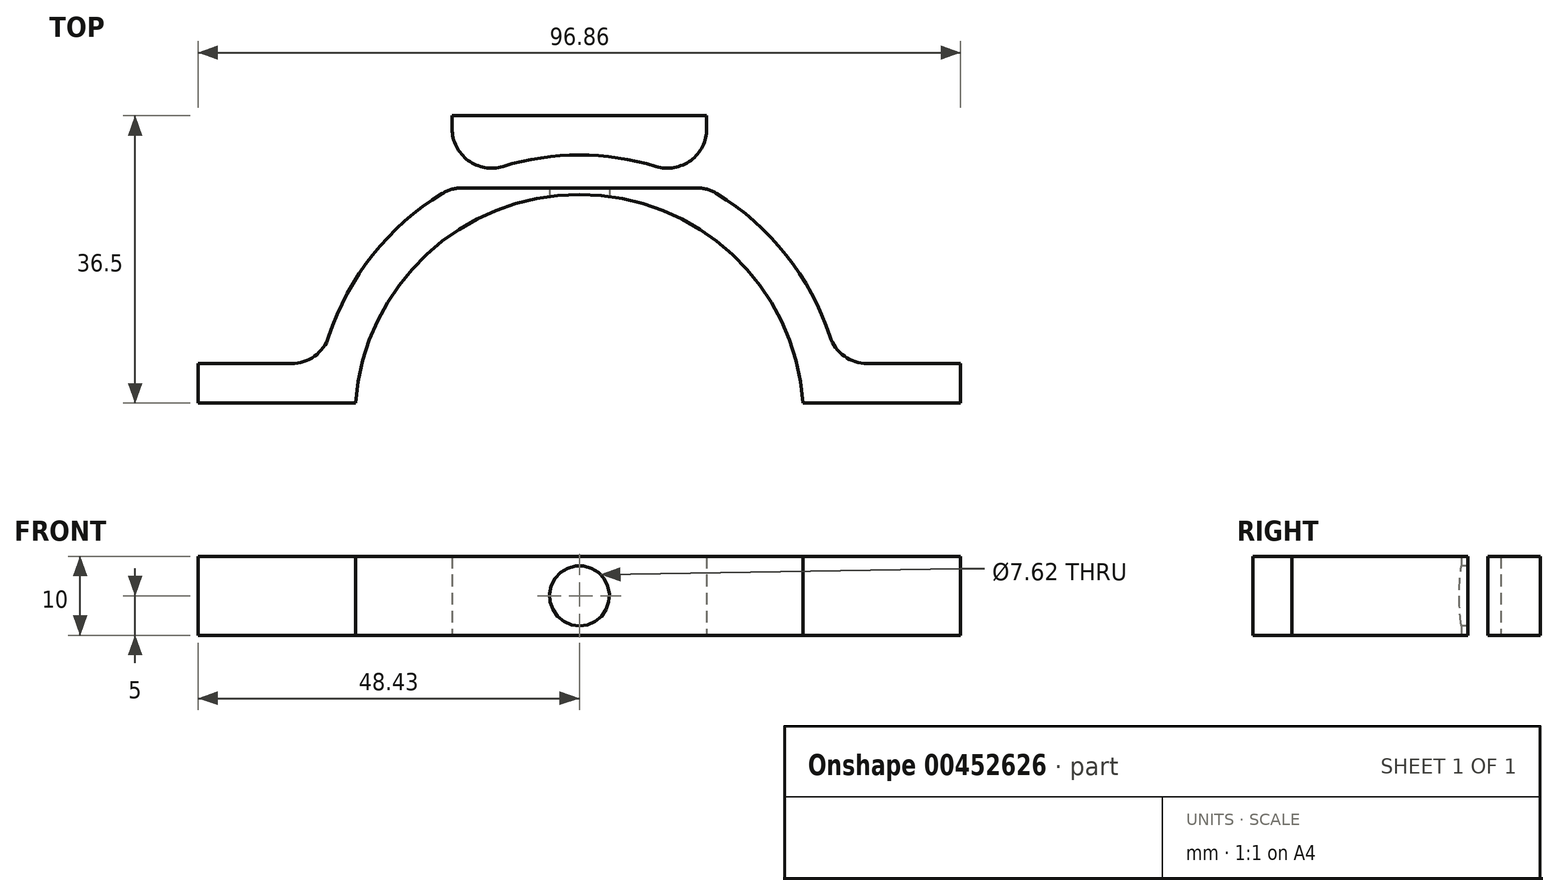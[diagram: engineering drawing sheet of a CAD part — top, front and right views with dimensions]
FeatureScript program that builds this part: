
annotation { "Feature Type Name" : "Feature", "Feature Type Description" : "" }
export const myFeature = defineFeature(function(context is Context, id is Id, definition is map)
    precondition{}
    {
        {
            var Q0;
            Q0=qCreatedBy(makeId("Top.planeOp"),FACE);
            var sketch = newSketch(context, id + "F0", { "sketchPlane" : qUnion([Q0])});
            skCircle(sketch, "E0", {"center": v(0, 0) * mm, "radius": 28.5 * mm, "construction": true});
            skLineSegment(sketch, "E1", {"start": v(-71.53, 0) * mm, "end": v(71.36, 0) * mm, "construction": true});
            skLineSegment(sketch, "E2", {"start": v(-71.7, 2) * mm, "end": v(71.19, 2) * mm, "construction": true});
            skArc(sketch, "E3", {"start": v(28.43, 2) * mm, "mid": v(0, 28.5) * mm, "end": v(-28.43, 2) * mm});
            skArc(sketch, "E4", {"start": v(33.44, 2) * mm, "mid": v(0, 33.5) * mm, "end": v(-33.44, 2) * mm});
            skLineSegment(sketch, "E5", {"start": v(-33.44, 2) * mm, "end": v(-28.43, 2) * mm});
            skLineSegment(sketch, "E6", {"start": v(28.43, 2) * mm, "end": v(33.44, 2) * mm});
            skLineSegment(sketch, "E7.bottom", {"start": v(-28.43, 2) * mm, "end": v(-48.43, 2) * mm});
            skLineSegment(sketch, "E7.top", {"start": v(-28.43, 7) * mm, "end": v(-48.43, 7) * mm});
            skLineSegment(sketch, "E7.left", {"start": v(-28.43, 2) * mm, "end": v(-28.43, 7) * mm});
            skLineSegment(sketch, "E7.right", {"start": v(-48.43, 2) * mm, "end": v(-48.43, 7) * mm});
            skLineSegment(sketch, "E8.bottom", {"start": v(28.43, 2) * mm, "end": v(48.43, 2) * mm});
            skLineSegment(sketch, "E8.top", {"start": v(28.43, 7) * mm, "end": v(48.43, 7) * mm});
            skLineSegment(sketch, "E8.left", {"start": v(28.43, 2) * mm, "end": v(28.43, 7) * mm});
            skLineSegment(sketch, "E8.right", {"start": v(48.43, 2) * mm, "end": v(48.43, 7) * mm});
            skLineSegment(sketch, "E9.bottom", {"start": v(-16.17, 33.5) * mm, "end": v(16.17, 33.5) * mm});
            skLineSegment(sketch, "E9.top", {"start": v(-16.17, 29.34) * mm, "end": v(16.17, 29.34) * mm});
            skLineSegment(sketch, "E9.left", {"start": v(-16.17, 33.5) * mm, "end": v(-16.17, 29.34) * mm});
            skLineSegment(sketch, "E9.right", {"start": v(16.17, 33.5) * mm, "end": v(16.17, 29.34) * mm});
            skPoint(sketch, "E10", {"position": v(0, 33.5) * mm});
            skLineSegment(sketch, "E11.top", {"start": v(-16.17, 23.47) * mm, "end": v(16.17, 23.47) * mm});
            skLineSegment(sketch, "E11.left", {"start": v(-16.17, 29.34) * mm, "end": v(-16.17, 23.47) * mm});
            skLineSegment(sketch, "E11.right", {"start": v(16.17, 29.34) * mm, "end": v(16.17, 23.47) * mm});
            skLineSegment(sketch, "E12.top", {"start": v(-16.17, 38.5) * mm, "end": v(16.17, 38.5) * mm});
            skLineSegment(sketch, "E12.left", {"start": v(-16.17, 33.5) * mm, "end": v(-16.17, 38.5) * mm});
            skLineSegment(sketch, "E12.right", {"start": v(16.17, 33.5) * mm, "end": v(16.17, 38.5) * mm});
            skSolve(sketch);
        }
        {
            var Q0;
            Q0=makeQuery(id+"F0.imprint","IMPRINT",FACE,{"disambiguationData":[TD([[makeQuery(id+"F0.imprint","IMPRINT",EDGE,{"derivedFrom":sQuery(id+"F0.wireOp",EDGE,"E3")}),-1.0]])]});
            var Q1;
            {var subQ5=sQuery(id+"F0.wireOp",EDGE,"E7.right");Q1=makeQuery(id+"F0.imprint","IMPRINT",FACE,{"disambiguationData":[TD([[makeQuery(id+"F0.imprint","IMPRINT",EDGE,{"derivedFrom":subQ5}),-1.0]])]});}
            var Q2;
            {var subQ5=sQuery(id+"F0.wireOp",EDGE,"E7.left");Q2=makeQuery(id+"F0.imprint","IMPRINT",FACE,{"disambiguationData":[TD([[makeQuery(id+"F0.imprint","IMPRINT",EDGE,{"derivedFrom":subQ5}),1.0]])]});}
            var Q3;
            {var subQ5=sQuery(id+"F0.wireOp",EDGE,"E8.left");Q3=makeQuery(id+"F0.imprint","IMPRINT",FACE,{"disambiguationData":[TD([[makeQuery(id+"F0.imprint","IMPRINT",EDGE,{"derivedFrom":subQ5}),-1.0]])]});}
            var Q4;
            {var subQ5=sQuery(id+"F0.wireOp",EDGE,"E8.right");Q4=makeQuery(id+"F0.imprint","IMPRINT",FACE,{"disambiguationData":[TD([[makeQuery(id+"F0.imprint","IMPRINT",EDGE,{"derivedFrom":subQ5}),1.0]])]});}
            var Q5;
            {var subQ0=sQuery(id+"F0.wireOp",EDGE,"E9.left");Q5=makeQuery(id+"F0.imprint","IMPRINT",FACE,{"disambiguationData":[TD([[makeQuery(id+"F0.imprint","IMPRINT",EDGE,{"derivedFrom":subQ0}),1.0]])]});}
            var Q6;
            {var subQ0=sQuery(id+"F0.wireOp",EDGE,"E9.right");Q6=makeQuery(id+"F0.imprint","IMPRINT",FACE,{"disambiguationData":[TD([[makeQuery(id+"F0.imprint","IMPRINT",EDGE,{"derivedFrom":subQ0}),-1.0]])]});}
            var Q7;
            {var subQ0=sQuery(id+"F0.wireOp",EDGE,"E7.left");Q7=makeQuery(id+"F0.imprint","IMPRINT",FACE,{"disambiguationData":[TD([[makeQuery(id+"F0.imprint","IMPRINT",EDGE,{"derivedFrom":subQ0}),-1.0]])]});}
            var Q8;
            {var subQ0=sQuery(id+"F0.wireOp",EDGE,"E9.top");var subQ4=sQuery(id+"F0.wireOp",EDGE,"E3");var subQ7=makeQuery(id+"F0.imprint","INTERSECT",VERTEX,{"disambiguationData":[OD(0.0)],"derivedFrom":[subQ4,subQ0]});Q8=makeQuery(id+"F0.imprint","IMPRINT",FACE,{"disambiguationData":[TD([[makeQuery(id+"F0.imprint","IMPRINT",EDGE,{"disambiguationData":[TD([[subQ7,-1.0]])],"derivedFrom":subQ4}),-1.0]])]});}
            var Q9;
            {var subQ0=sQuery(id+"F0.wireOp",EDGE,"E11.top");Q9=makeQuery(id+"F0.imprint","IMPRINT",FACE,{"disambiguationData":[TD([[makeQuery(id+"F0.imprint","IMPRINT",EDGE,{"derivedFrom":subQ0}),1.0]])]});}
            var Q10;
            {var subQ0=sQuery(id+"F0.wireOp",EDGE,"E8.left");Q10=makeQuery(id+"F0.imprint","IMPRINT",FACE,{"disambiguationData":[TD([[makeQuery(id+"F0.imprint","IMPRINT",EDGE,{"derivedFrom":subQ0}),1.0]])]});}
            var Q11;
            Q11=makeQuery(id+"F0.imprint","IMPRINT",FACE,{"disambiguationData":[TD([[makeQuery(id+"F0.imprint","IMPRINT",EDGE,{"derivedFrom":sQuery(id+"F0.wireOp",EDGE,"E12.top")}),-1.0]])]});
            var Q12;
            {var subQ0=sQuery(id+"F0.wireOp",EDGE,"E9.top");Q12=makeQuery(id+"F0.imprint","IMPRINT",FACE,{"disambiguationData":[TD([[makeQuery(id+"F0.imprint","IMPRINT",EDGE,{"derivedFrom":subQ0}),1.0]])]});}
            extrude(context, id + "F1", {"entities" : qUnion([Q0, Q1, Q2, Q3, Q4, Q5, Q6, Q7, Q8, Q9, Q10, Q11, Q12]), "depth" : 10 * mm});
        }
        {
            var Q0;
            Q0=makeQuery(id+"F1.opExtrude","SWEPT_FACE",FACE,{"disambiguationData":[OSD([sQuery(id+"F0.wireOp",EDGE,"E11.top")])]});
            var sketch = newSketch(context, id + "F2", { "sketchPlane" : qUnion([Q0])});
            skPoint(sketch, "E13", {"position": v(0, 5) * mm});
            skLineSegment(sketch, "E14", {"start": v(0, 0) * mm, "end": v(0, 10) * mm, "construction": true});
            skSolve(sketch);
        }
        {
            var Q0;
            Q0=sQuery(id+"F2.wireOp",VERTEX,"E13");
            var Q1;
            Q1=makeQuery(id+"F1.opExtrude","SWEPT_BODY",BODY,{"disambiguationData":[OSD([sQuery(id+"F0.wireOp",EDGE,"E3"),sQuery(id+"F0.wireOp",EDGE,"E4"),sQuery(id+"F0.wireOp",EDGE,"E7.bottom"),sQuery(id+"F0.wireOp",EDGE,"E7.top"),sQuery(id+"F0.wireOp",EDGE,"E7.right"),sQuery(id+"F0.wireOp",EDGE,"E8.bottom"),sQuery(id+"F0.wireOp",EDGE,"E8.top"),sQuery(id+"F0.wireOp",EDGE,"E8.right"),sQuery(id+"F0.wireOp",EDGE,"E9.bottom"),sQuery(id+"F0.wireOp",EDGE,"E9.left"),sQuery(id+"F0.wireOp",EDGE,"E9.right"),sQuery(id+"F0.wireOp",EDGE,"E9.top"),sQuery(id+"F0.wireOp",EDGE,"E11.top")])]});
            hole(context, id + "F3", {"style" : HoleStyle.C_BORE, "endStyle" : HoleEndStyle.THROUGH, "holeDiameter" : 3.56 * mm, "cBoreDiameter" : 7.62 * mm, "cBoreDepth" : 10 * mm, "isTappedThrough" : true, "tappedDepth" : 12 * mm, "tapClearance" : 3, "locations" : qUnion([Q0]), "scope" : qUnion([Q1])});
        }
        {
            var Q0;
            {var subQ0=sQuery(id+"F0.wireOp",EDGE,"E11.top");Q0=makeQuery(id+"F0.imprint","IMPRINT",FACE,{"disambiguationData":[TD([[makeQuery(id+"F0.imprint","IMPRINT",EDGE,{"derivedFrom":subQ0}),1.0]])]});}
            extrude(context, id + "F4", {"entities" : qUnion([Q0]), "operationType" : NewBodyOperationType.REMOVE, "endBound" : BoundingType.THROUGH_ALL, "depth" : 25 * mm});
        }
        {
            var Q0;
            Q0=makeQuery(id+"F1.opExtrude","SWEPT_FACE",FACE,{"disambiguationData":[OSD([sQuery(id+"F0.wireOp",EDGE,"E7.bottom")])]});
            var sketch = newSketch(context, id + "F5", { "sketchPlane" : qUnion([Q0])});
            skPoint(sketch, "E15", {"position": v(-39.12, 4.78) * mm});
            skPoint(sketch, "E16.MirrorP", {"position": v(39.12, 4.78) * mm});
            skSolve(sketch);
        }
        {
            var Q0;
            Q0=sQuery(id+"F5.wireOp",VERTEX,"E15");
            var Q1;
            Q1=sQuery(id+"F5.wireOp",VERTEX,"E16.MirrorP");
            var Q2;
            Q2=makeQuery(id+"F1.opExtrude","SWEPT_BODY",BODY,{"disambiguationData":[OSD([sQuery(id+"F0.wireOp",EDGE,"E3"),sQuery(id+"F0.wireOp",EDGE,"E4"),sQuery(id+"F0.wireOp",EDGE,"E7.bottom"),sQuery(id+"F0.wireOp",EDGE,"E7.top"),sQuery(id+"F0.wireOp",EDGE,"E7.right"),sQuery(id+"F0.wireOp",EDGE,"E8.bottom"),sQuery(id+"F0.wireOp",EDGE,"E8.top"),sQuery(id+"F0.wireOp",EDGE,"E8.right"),sQuery(id+"F0.wireOp",EDGE,"E9.left"),sQuery(id+"F0.wireOp",EDGE,"E9.right"),sQuery(id+"F0.wireOp",EDGE,"E9.top"),sQuery(id+"F0.wireOp",EDGE,"E11.top"),sQuery(id+"F0.wireOp",EDGE,"E12.top"),sQuery(id+"F0.wireOp",EDGE,"E12.left"),sQuery(id+"F0.wireOp",EDGE,"E12.right")])]});
            hole(context, id + "F6", {"style" : HoleStyle.SIMPLE, "endStyle" : HoleEndStyle.THROUGH, "holeDiameter" : 3.56 * mm, "isTappedThrough" : true, "tappedDepth" : 12 * mm, "tapClearance" : 3, "locations" : qUnion([Q0, Q1]), "scope" : qUnion([Q2])});
        }
        {
            var Q0;
            Q0=makeQuery(id+"F1.opExtrude","SWEPT_EDGE",EDGE,{"disambiguationData":[OSD([sQuery(id+"F0.wireOp",EDGE,"E4"),sQuery(id+"F0.wireOp",EDGE,"E7.top")])]});
            var Q1;
            Q1=makeQuery(id+"F1.opExtrude","SWEPT_EDGE",EDGE,{"disambiguationData":[OSD([sQuery(id+"F0.wireOp",EDGE,"E4"),sQuery(id+"F0.wireOp",EDGE,"E8.top")])]});
            var Q2;
            Q2=makeQuery(id+"F1.opExtrude","SWEPT_EDGE",EDGE,{"disambiguationData":[OSD([sQuery(id+"F0.wireOp",EDGE,"E4"),sQuery(id+"F0.wireOp",EDGE,"E9.right"),sQuery(id+"F0.wireOp",EDGE,"E9.top"),sQuery(id+"F0.wireOp",EDGE,"E11.right")])]});
            var Q3;
            Q3=makeQuery(id+"F1.opExtrude","SWEPT_EDGE",EDGE,{"disambiguationData":[OSD([sQuery(id+"F0.wireOp",EDGE,"E4"),sQuery(id+"F0.wireOp",EDGE,"E9.left"),sQuery(id+"F0.wireOp",EDGE,"E9.top"),sQuery(id+"F0.wireOp",EDGE,"E11.left")])]});
            fillet(context, id + "F7", {"entities" : qUnion([Q0, Q1, Q2, Q3]), "radius" : 5 * mm, "tangentPropagation" : true, "allowEdgeOverflow" : false});
        }
    });
